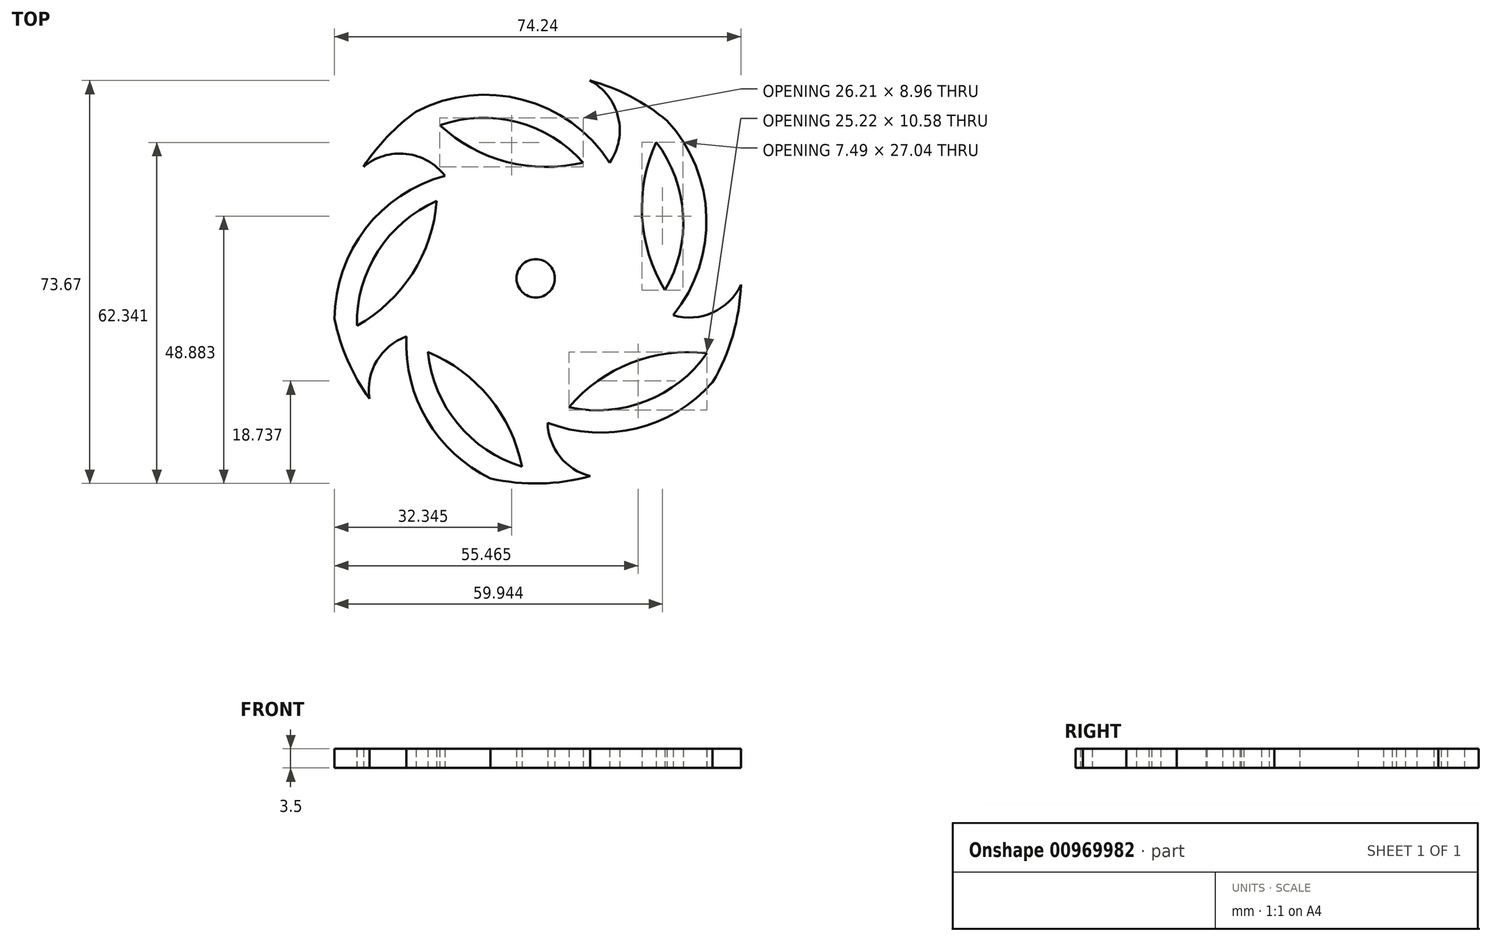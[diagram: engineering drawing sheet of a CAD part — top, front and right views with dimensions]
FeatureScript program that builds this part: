
annotation { "Feature Type Name" : "Feature", "Feature Type Description" : "" }
export const myFeature = defineFeature(function(context is Context, id is Id, definition is map)
    precondition{}
    {
        {
            var Q0;
            Q0=qCreatedBy(makeId("Top.planeOp"),FACE);
            var sketch = newSketch(context, id + "F0", { "sketchPlane" : qUnion([Q0])});
            skLineSegment(sketch, "E0.bottom", {"start": v(37.5, 37.5) * mm, "end": v(-37.5, 37.5) * mm});
            skLineSegment(sketch, "E0.top", {"start": v(37.5, -37.5) * mm, "end": v(-37.5, -37.5) * mm});
            skLineSegment(sketch, "E0.left", {"start": v(37.5, 37.5) * mm, "end": v(37.5, -37.5) * mm});
            skLineSegment(sketch, "E0.right", {"start": v(-37.5, 37.5) * mm, "end": v(-37.5, -37.5) * mm});
            skPoint(sketch, "E0.middle", {"position": v(0, 0) * mm});
            skCircle(sketch, "E1", {"center": v(0, 0) * mm, "radius": 3.5 * mm});
            skCircle(sketch, "E2", {"center": v(0, 0) * mm, "radius": 37.5 * mm});
            skArc(sketch, "E3", {"start": v(13.53, 21.16) * mm, "mid": v(-2.35, 32.66) * mm, "end": v(-21.84, 30.48) * mm});
            skArc(sketch, "E4", {"start": v(13.53, 21.16) * mm, "mid": v(15.06, 29.48) * mm, "end": v(9.89, 36.17) * mm});
            skArc(sketch, "E5", {"start": v(8.69, 21.16) * mm, "mid": v(-3.38, 28.55) * mm, "end": v(-17.52, 28) * mm});
            skArc(sketch, "E6", {"start": v(-17.52, 28) * mm, "mid": v(-5.27, 21.29) * mm, "end": v(8.69, 21.16) * mm});
            skArc(sketch, "E7.1.0", {"start": v(-16.6, 18.75) * mm, "mid": v(-32.44, 7.2) * mm, "end": v(-36.39, -12) * mm});
            skArc(sketch, "E7.1.1", {"start": v(-18.09, 14.15) * mm, "mid": v(-28.84, 4.95) * mm, "end": v(-32.69, -8.66) * mm});
            skArc(sketch, "E7.1.2", {"start": v(-16.6, 18.75) * mm, "mid": v(-24.03, 22.78) * mm, "end": v(-32, 19.93) * mm});
            skArc(sketch, "E7.1.3", {"start": v(-32.69, -8.66) * mm, "mid": v(-22.52, 0.9) * mm, "end": v(-18.09, 14.15) * mm});
            skArc(sketch, "E7.2.0", {"start": v(-23.6, -10.64) * mm, "mid": v(-17.52, -29.28) * mm, "end": v(-0.47, -38.97) * mm});
            skArc(sketch, "E7.2.1", {"start": v(-19.69, -13.48) * mm, "mid": v(-14.27, -26.55) * mm, "end": v(-2.5, -34.42) * mm});
            skArc(sketch, "E7.2.2", {"start": v(-23.6, -10.64) * mm, "mid": v(-29.74, -16.47) * mm, "end": v(-29.48, -24.92) * mm});
            skArc(sketch, "E7.2.3", {"start": v(-2.5, -34.42) * mm, "mid": v(-8.47, -21.8) * mm, "end": v(-19.69, -13.48) * mm});
            skArc(sketch, "E7.3.0", {"start": v(2.18, -26.4) * mm, "mid": v(21.79, -26.36) * mm, "end": v(36.27, -13.14) * mm});
            skArc(sketch, "E7.3.1", {"start": v(6.1, -23.55) * mm, "mid": v(20.2, -22.43) * mm, "end": v(31.32, -13.67) * mm});
            skArc(sketch, "E7.3.2", {"start": v(2.18, -26.4) * mm, "mid": v(5.83, -34.03) * mm, "end": v(13.95, -36.4) * mm});
            skArc(sketch, "E7.3.3", {"start": v(31.32, -13.67) * mm, "mid": v(17.47, -15.44) * mm, "end": v(6.1, -23.55) * mm});
            skArc(sketch, "E7.4.0", {"start": v(25.13, -6.74) * mm, "mid": v(31.16, 11.92) * mm, "end": v(23.06, 29.78) * mm});
            skArc(sketch, "E7.4.1", {"start": v(23.63, -2.14) * mm, "mid": v(26.93, 11.63) * mm, "end": v(22.04, 24.9) * mm});
            skArc(sketch, "E7.4.2", {"start": v(25.13, -6.74) * mm, "mid": v(33.52, -5.63) * mm, "end": v(38.28, 1.36) * mm});
            skArc(sketch, "E7.4.3", {"start": v(22.04, 24.9) * mm, "mid": v(19.44, 11.18) * mm, "end": v(23.63, -2.14) * mm});
            skSolve(sketch);
        }
        {
            var Q0;
            Q0=makeQuery(id+"F0.imprint","IMPRINT",FACE,{"disambiguationData":[TD([[makeQuery(id+"F0.imprint","IMPRINT",EDGE,{"derivedFrom":sQuery(id+"F0.wireOp",EDGE,"E1")}),-1.0]])]});
            extrude(context, id + "F1", {"entities" : qUnion([Q0]), "depth" : 3.5 * mm, "offsetDistance" : 25 * mm});
        }
    });
